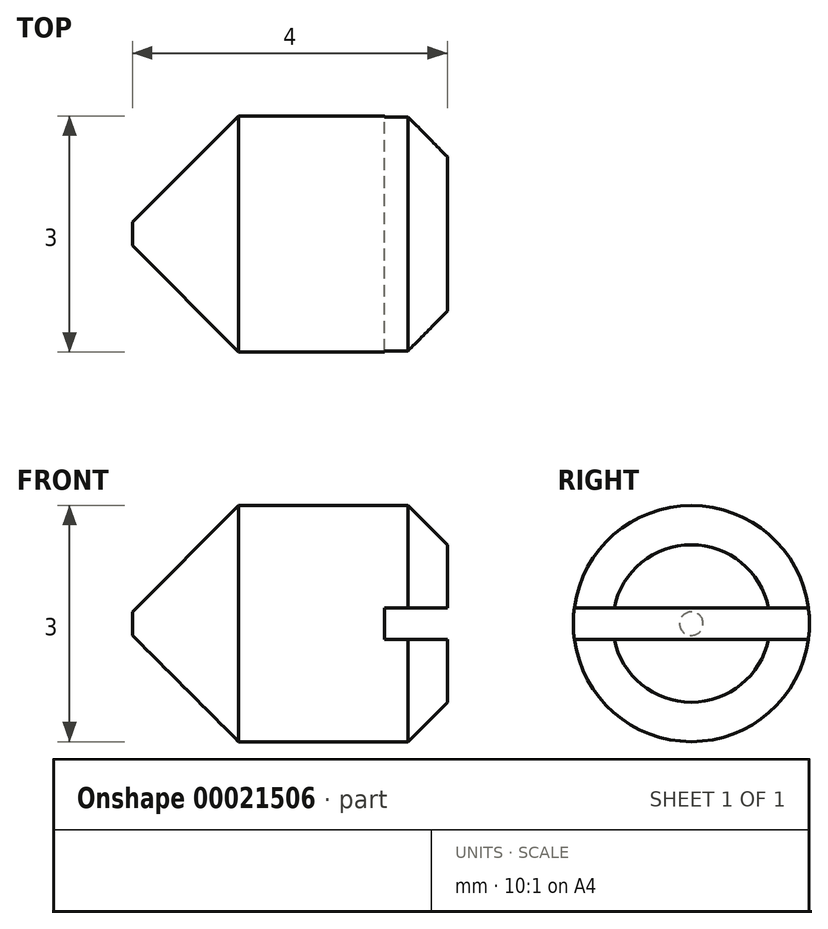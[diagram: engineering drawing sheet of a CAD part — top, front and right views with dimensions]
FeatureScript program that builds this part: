
annotation { "Feature Type Name" : "Feature", "Feature Type Description" : "" }
export const myFeature = defineFeature(function(context is Context, id is Id, definition is map)
    precondition{}
    {
        {
            var Q0;
            Q0=qCreatedBy(makeId("Front.planeOp"),FACE);
            var sketch = newSketch(context, id + "F2", { "sketchPlane" : qUnion([Q0])});
            skLineSegment(sketch, "E0", {"start": v(1.35, 1.5) * mm, "end": v(4, 1.5) * mm});
            skLineSegment(sketch, "E1", {"start": v(4, 1.5) * mm, "end": v(4, 0) * mm});
            skLineSegment(sketch, "E2", {"start": v(4, 0) * mm, "end": v(0, 0) * mm});
            skLineSegment(sketch, "E3", {"start": v(1.35, 1.5) * mm, "end": v(0, 0.15) * mm});
            skLineSegment(sketch, "E4", {"start": v(0, 0.15) * mm, "end": v(0, 0) * mm});
            skSolve(sketch);
        }
        {
            var Q0;
            Q0=qSketchRegion(id+"F2",true);
            var Q1;
            Q1=sQuery(id+"F2.wireOp",EDGE,"E2");
            revolve(context, id + "F3", {"entities" : qUnion([Q0]), "axis" : qUnion([Q1]), "revolveType" : RevolveType.FULL});
        }
        {
            var Q0;
            Q0=makeQuery(id+"F3.opRevolve","SWEPT_FACE",FACE,{"disambiguationData":[OSD([sQuery(id+"F2.wireOp",EDGE,"E1")])]});
            var sketch = newSketch(context, id + "F0", { "sketchPlane" : qUnion([Q0])});
            skLineSegment(sketch, "E5.bottom", {"start": v(-1.5, 0.2) * mm, "end": v(1.5, 0.2) * mm});
            skLineSegment(sketch, "E5.top", {"start": v(-1.5, -0.2) * mm, "end": v(1.5, -0.2) * mm});
            skLineSegment(sketch, "E5.left", {"start": v(-1.5, 0.2) * mm, "end": v(-1.5, -0.2) * mm});
            skLineSegment(sketch, "E5.right", {"start": v(1.5, 0.2) * mm, "end": v(1.5, -0.2) * mm});
            skLineSegment(sketch, "E6", {"start": v(-1.5, 0) * mm, "end": v(1.5, 0) * mm, "construction": true});
            skSolve(sketch);
        }
        {
            var Q0;
            Q0=makeQuery(id+"F3.opRevolve","SWEPT_EDGE",EDGE,{"disambiguationData":[OSD([sQuery(id+"F2.wireOp",EDGE,"E0"),sQuery(id+"F2.wireOp",EDGE,"E1")])]});
            chamfer(context, id + "F1", {"entities" : qUnion([Q0]), "width" : 0.5 * mm, "tangentPropagation" : true});
        }
        {
            var Q0;
            Q0=qSketchRegion(id+"F0",true);
            extrude(context, id + "F4", {"entities" : qUnion([Q0]), "operationType" : NewBodyOperationType.REMOVE, "oppositeDirection" : true, "depth" : 0.8 * mm});
        }
    });
